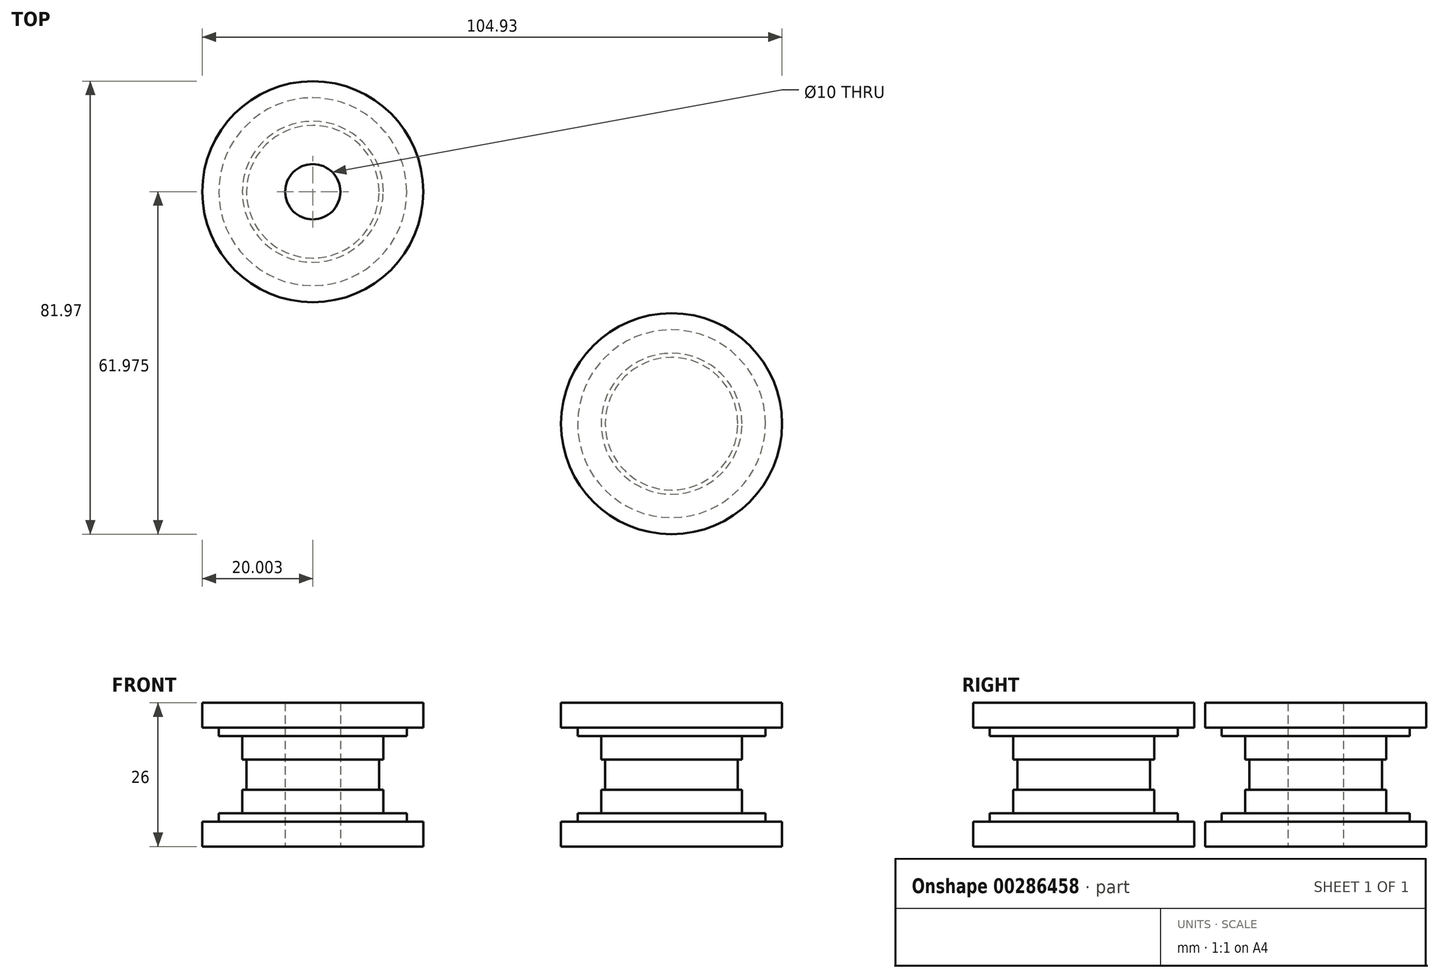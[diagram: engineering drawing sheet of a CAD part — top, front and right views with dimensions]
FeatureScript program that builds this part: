
annotation { "Feature Type Name" : "Feature", "Feature Type Description" : "" }
export const myFeature = defineFeature(function(context is Context, id is Id, definition is map)
    precondition{}
    {
        {
            var Q0;
            Q0=qCreatedBy(makeId("Top.planeOp"),FACE);
            var sketch = newSketch(context, id + "F0", { "sketchPlane" : qUnion([Q0])});
            skCircle(sketch, "E0", {"center": v(0, 0) * mm, "radius": 20 * mm});
            skSolve(sketch);
        }
        {
            var Q0;
            Q0=makeQuery(id+"F0.imprint","IMPRINT",FACE,{"disambiguationData":[TD([[makeQuery(id+"F0.imprint","IMPRINT",EDGE,{"derivedFrom":sQuery(id+"F0.wireOp",EDGE,"E0")}),1.0]])]});
            extrude(context, id + "F1", {"entities" : qUnion([Q0]), "depth" : 4.5 * mm});
        }
        {
            var Q0;
            Q0=qCreatedBy(makeId("Top.planeOp"),FACE);
            var sketch = newSketch(context, id + "F2", { "sketchPlane" : qUnion([Q0])});
            skCircle(sketch, "E1", {"center": v(0, 0) * mm, "radius": 17 * mm});
            skSolve(sketch);
        }
        {
            var Q0;
            Q0 = qSketchRegion(id + "F2", true);
            extrude(context, id + "F3", {"entities" : qUnion([Q0]), "operationType" : NewBodyOperationType.ADD, "depth" : 6 * mm});
        }
        {
            var Q0;
            Q0=qCreatedBy(makeId("Top.planeOp"),FACE);
            var sketch = newSketch(context, id + "F4", { "sketchPlane" : qUnion([Q0])});
            skCircle(sketch, "E2", {"center": v(0, 0) * mm, "radius": 12.75 * mm});
            skSolve(sketch);
        }
        {
            var Q0;
            Q0 = qSketchRegion(id + "F4", true);
            extrude(context, id + "F5", {"entities" : qUnion([Q0]), "operationType" : NewBodyOperationType.ADD, "depth" : 10.25 * mm});
        }
        {
            var Q0;
            Q0=qCreatedBy(makeId("Top.planeOp"),FACE);
            var sketch = newSketch(context, id + "F6", { "sketchPlane" : qUnion([Q0])});
            skCircle(sketch, "E3", {"center": v(0, 0) * mm, "radius": 12 * mm});
            skSolve(sketch);
        }
        {
            var Q0;
            Q0 = qSketchRegion(id + "F6", true);
            extrude(context, id + "F7", {"entities" : qUnion([Q0]), "operationType" : NewBodyOperationType.ADD, "depth" : 15.75 * mm});
        }
        {
            var Q0;
            Q0=makeQuery(id+"F7.opExtrude","CAP_FACE",FACE,{"disambiguationData":[OSD([sQuery(id+"F6.wireOp",EDGE,"E3")])],"isStart":false});
            var sketch = newSketch(context, id + "F8", { "sketchPlane" : qUnion([Q0])});
            skCircle(sketch, "E4", {"center": v(0, 0) * mm, "radius": 12.75 * mm});
            skSolve(sketch);
        }
        {
            var Q0;
            Q0 = qSketchRegion(id + "F8", true);
            extrude(context, id + "F9", {"entities" : qUnion([Q0]), "operationType" : NewBodyOperationType.ADD, "depth" : 4.25 * mm});
        }
        {
            var Q0;
            Q0=makeQuery(id+"F9.opExtrude","CAP_FACE",FACE,{"disambiguationData":[OSD([sQuery(id+"F8.wireOp",EDGE,"E4")])],"isStart":false});
            var sketch = newSketch(context, id + "F10", { "sketchPlane" : qUnion([Q0])});
            skCircle(sketch, "E5", {"center": v(0, 0) * mm, "radius": 17 * mm});
            skSolve(sketch);
        }
        {
            var Q0;
            Q0 = qSketchRegion(id + "F10", true);
            extrude(context, id + "F11", {"entities" : qUnion([Q0]), "operationType" : NewBodyOperationType.ADD, "depth" : 1.5 * mm});
        }
        {
            var Q0;
            Q0=makeQuery(id+"F11.opExtrude","CAP_FACE",FACE,{"disambiguationData":[OSD([sQuery(id+"F10.wireOp",EDGE,"E5")])],"isStart":false});
            var sketch = newSketch(context, id + "F12", { "sketchPlane" : qUnion([Q0])});
            skCircle(sketch, "E6", {"center": v(0, 0) * mm, "radius": 20 * mm});
            skSolve(sketch);
        }
        {
            var Q0;
            Q0 = qSketchRegion(id + "F12", true);
            extrude(context, id + "F13", {"entities" : qUnion([Q0]), "operationType" : NewBodyOperationType.ADD, "depth" : 4.5 * mm});
        }
        {
            var Q0;
            Q0=qCreatedBy(makeId("Top.planeOp"),FACE);
            var sketch = newSketch(context, id + "F14", { "sketchPlane" : qUnion([Q0])});
            skCircle(sketch, "E7", {"center": v(-64.93, 41.97) * mm, "radius": 20 * mm});
            skCircle(sketch, "E8", {"center": v(-64.93, 41.97) * mm, "radius": 5 * mm});
            skSolve(sketch);
        }
        {
            var Q0;
            Q0 = qSketchRegion(id + "F14", true);
            extrude(context, id + "F15", {"entities" : qUnion([Q0]), "depth" : 4.5 * mm});
        }
        {
            var Q0;
            Q0=makeQuery(id+"F15.opExtrude","CAP_FACE",FACE,{"disambiguationData":[OSD([sQuery(id+"F14.wireOp",EDGE,"E7"),sQuery(id+"F14.wireOp",EDGE,"E8")])],"isStart":false});
            var sketch = newSketch(context, id + "F16", { "sketchPlane" : qUnion([Q0])});
            skCircle(sketch, "E9", {"center": v(-64.93, 41.97) * mm, "radius": 17 * mm});
            skCircle(sketch, "E10", {"center": v(-64.93, 41.97) * mm, "radius": 5 * mm});
            skSolve(sketch);
        }
        {
            var Q0;
            Q0 = qSketchRegion(id + "F16", true);
            extrude(context, id + "F17", {"entities" : qUnion([Q0]), "operationType" : NewBodyOperationType.ADD, "depth" : 1.5 * mm});
        }
        {
            var Q0;
            Q0=makeQuery(id+"F17.opExtrude","CAP_FACE",FACE,{"disambiguationData":[OSD([sQuery(id+"F16.wireOp",EDGE,"E9"),sQuery(id+"F16.wireOp",EDGE,"E10")])],"isStart":false});
            var sketch = newSketch(context, id + "F18", { "sketchPlane" : qUnion([Q0])});
            skCircle(sketch, "E11", {"center": v(-64.93, 41.97) * mm, "radius": 12.75 * mm});
            skCircle(sketch, "E12", {"center": v(-64.93, 41.97) * mm, "radius": 5 * mm});
            skSolve(sketch);
        }
        {
            var Q0;
            Q0 = qSketchRegion(id + "F18", true);
            extrude(context, id + "F19", {"entities" : qUnion([Q0]), "operationType" : NewBodyOperationType.ADD, "depth" : 4.25 * mm});
        }
        {
            var Q0;
            Q0=makeQuery(id+"F19.opExtrude","CAP_FACE",FACE,{"disambiguationData":[OSD([sQuery(id+"F18.wireOp",EDGE,"E11"),sQuery(id+"F18.wireOp",EDGE,"E12")])],"isStart":false});
            var sketch = newSketch(context, id + "F20", { "sketchPlane" : qUnion([Q0])});
            skCircle(sketch, "E13", {"center": v(-64.93, 41.97) * mm, "radius": 12 * mm});
            skCircle(sketch, "E14", {"center": v(-64.93, 41.97) * mm, "radius": 5 * mm});
            skSolve(sketch);
        }
        {
            var Q0;
            Q0 = qSketchRegion(id + "F20", true);
            extrude(context, id + "F21", {"entities" : qUnion([Q0]), "operationType" : NewBodyOperationType.ADD, "depth" : 5.5 * mm});
        }
        {
            var Q0;
            Q0=makeQuery(id+"F21.opExtrude","CAP_FACE",FACE,{"disambiguationData":[OSD([sQuery(id+"F20.wireOp",EDGE,"E13"),sQuery(id+"F20.wireOp",EDGE,"E14")])],"isStart":false});
            var sketch = newSketch(context, id + "F22", { "sketchPlane" : qUnion([Q0])});
            skCircle(sketch, "E15", {"center": v(-64.93, 41.97) * mm, "radius": 12.75 * mm});
            skCircle(sketch, "E16", {"center": v(-64.93, 41.97) * mm, "radius": 5 * mm});
            skSolve(sketch);
        }
        {
            var Q0;
            Q0 = qSketchRegion(id + "F22", true);
            extrude(context, id + "F23", {"entities" : qUnion([Q0]), "operationType" : NewBodyOperationType.ADD, "depth" : 4.25 * mm});
        }
        {
            var Q0;
            Q0=makeQuery(id+"F23.opExtrude","CAP_FACE",FACE,{"disambiguationData":[OSD([sQuery(id+"F22.wireOp",EDGE,"E15"),sQuery(id+"F22.wireOp",EDGE,"E16")])],"isStart":false});
            var sketch = newSketch(context, id + "F24", { "sketchPlane" : qUnion([Q0])});
            skCircle(sketch, "E17", {"center": v(-64.93, 41.97) * mm, "radius": 17 * mm});
            skCircle(sketch, "E18", {"center": v(-64.93, 41.97) * mm, "radius": 5 * mm});
            skSolve(sketch);
        }
        {
            var Q0;
            Q0 = qSketchRegion(id + "F24", true);
            extrude(context, id + "F25", {"entities" : qUnion([Q0]), "operationType" : NewBodyOperationType.ADD, "depth" : 1.5 * mm});
        }
        {
            var Q0;
            Q0=makeQuery(id+"F25.opExtrude","CAP_FACE",FACE,{"disambiguationData":[OSD([sQuery(id+"F24.wireOp",EDGE,"E17"),sQuery(id+"F24.wireOp",EDGE,"E18")])],"isStart":false});
            var sketch = newSketch(context, id + "F26", { "sketchPlane" : qUnion([Q0])});
            skCircle(sketch, "E19", {"center": v(-64.93, 41.97) * mm, "radius": 20 * mm});
            skCircle(sketch, "E20", {"center": v(-64.93, 41.97) * mm, "radius": 5 * mm});
            skSolve(sketch);
        }
        {
            var Q0;
            Q0 = qSketchRegion(id + "F26", true);
            extrude(context, id + "F27", {"entities" : qUnion([Q0]), "operationType" : NewBodyOperationType.ADD, "depth" : 4.5 * mm});
        }
    });
